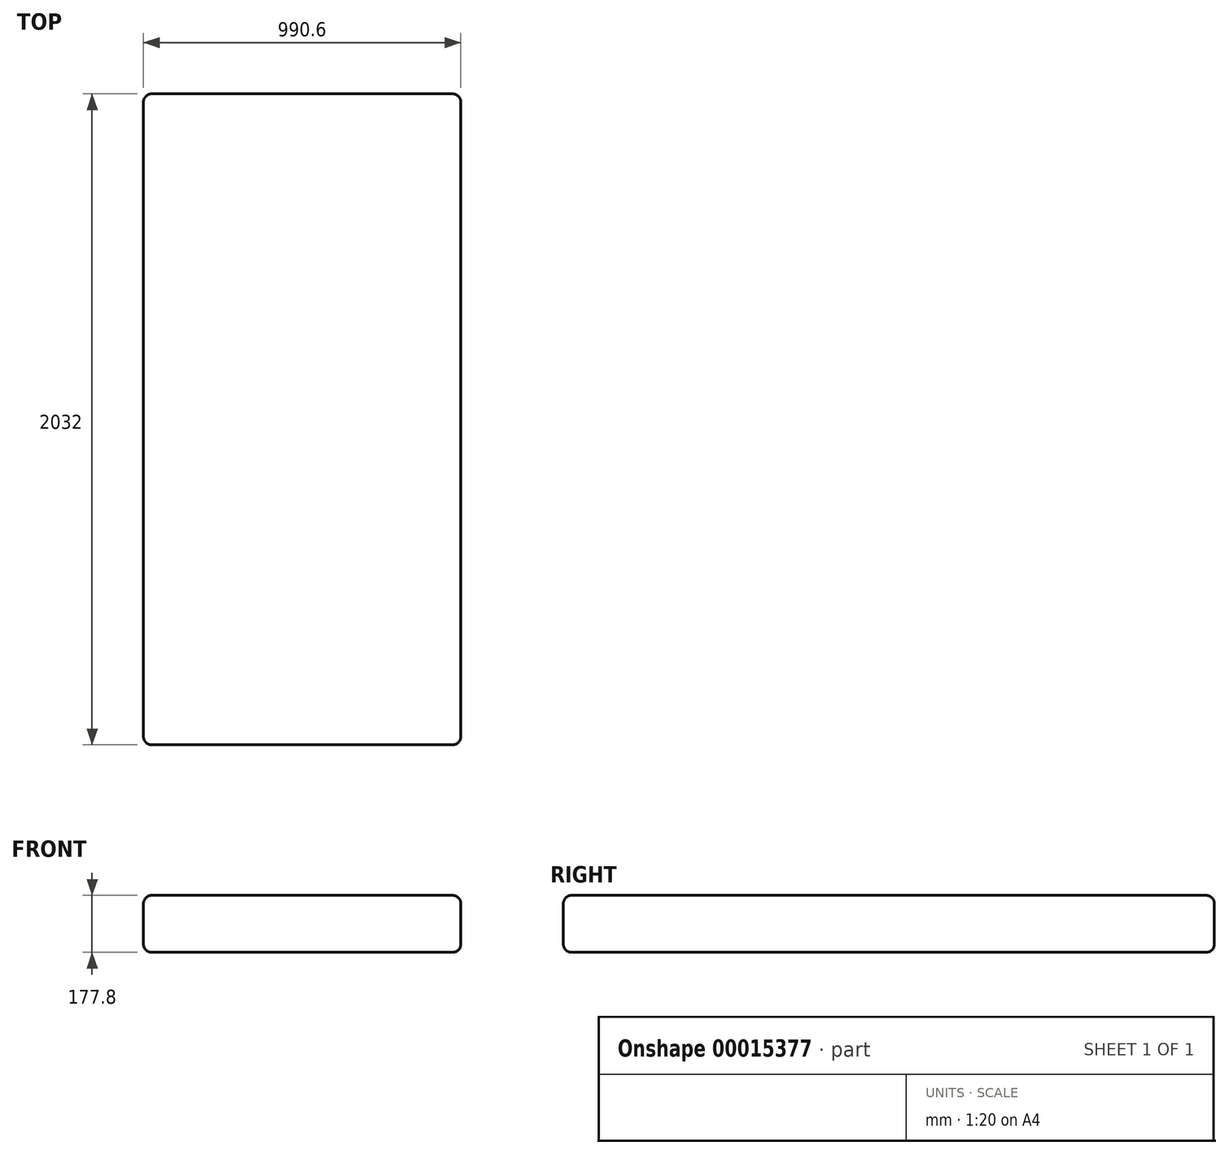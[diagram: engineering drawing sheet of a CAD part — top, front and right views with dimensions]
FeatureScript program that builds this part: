
annotation { "Feature Type Name" : "Feature", "Feature Type Description" : "" }
export const myFeature = defineFeature(function(context is Context, id is Id, definition is map)
    precondition{}
    {
        {
            var Q0;
            Q0=qCreatedBy(makeId("Top.planeOp"),FACE);
            var sketch = newSketch(context, id + "F0", { "sketchPlane" : qUnion([Q0])});
            skLineSegment(sketch, "E0.bottom", {"start": v(-495.25, -781.3) * mm, "end": v(495.35, -781.3) * mm});
            skLineSegment(sketch, "E0.top", {"start": v(-495.25, 1250.7) * mm, "end": v(495.35, 1250.7) * mm});
            skLineSegment(sketch, "E0.left", {"start": v(-495.25, -781.3) * mm, "end": v(-495.25, 1250.7) * mm});
            skLineSegment(sketch, "E0.right", {"start": v(495.35, -781.3) * mm, "end": v(495.35, 1250.7) * mm});
            skSolve(sketch);
        }
        {
            var Q0;
            Q0=qSketchRegion(id+"F0",true);
            extrude(context, id + "F1", {"entities" : qUnion([Q0]), "depth" : 177.8 * mm});
        }
        {
            var Q0;
            Q0=makeQuery(id+"F1.opExtrude","CAP_EDGE",EDGE,{"disambiguationData":[OSD([sQuery(id+"F0.wireOp",EDGE,"E0.bottom")])],"isStart":false});
            var Q1;
            Q1=makeQuery(id+"F1.opExtrude","CAP_EDGE",EDGE,{"disambiguationData":[OSD([sQuery(id+"F0.wireOp",EDGE,"E0.right")])],"isStart":false});
            var Q2;
            Q2=makeQuery(id+"F1.opExtrude","SWEPT_EDGE",EDGE,{"disambiguationData":[OSD([sQuery(id+"F0.wireOp",EDGE,"E0.bottom"),sQuery(id+"F0.wireOp",EDGE,"E0.right")])]});
            var Q3;
            Q3=makeQuery(id+"F1.opExtrude","SWEPT_EDGE",EDGE,{"disambiguationData":[OSD([sQuery(id+"F0.wireOp",EDGE,"E0.bottom"),sQuery(id+"F0.wireOp",EDGE,"E0.left")])]});
            var Q4;
            Q4=makeQuery(id+"F1.opExtrude","SWEPT_EDGE",EDGE,{"disambiguationData":[OSD([sQuery(id+"F0.wireOp",EDGE,"E0.top"),sQuery(id+"F0.wireOp",EDGE,"E0.left")])]});
            var Q5;
            Q5=makeQuery(id+"F1.opExtrude","SWEPT_EDGE",EDGE,{"disambiguationData":[OSD([sQuery(id+"F0.wireOp",EDGE,"E0.top"),sQuery(id+"F0.wireOp",EDGE,"E0.right")])]});
            var Q6;
            Q6=makeQuery(id+"F1.opExtrude","CAP_EDGE",EDGE,{"disambiguationData":[OSD([sQuery(id+"F0.wireOp",EDGE,"E0.bottom")])],"isStart":true});
            var Q7;
            Q7=makeQuery(id+"F1.opExtrude","CAP_EDGE",EDGE,{"disambiguationData":[OSD([sQuery(id+"F0.wireOp",EDGE,"E0.top")])],"isStart":false});
            var Q8;
            Q8=makeQuery(id+"F1.opExtrude","CAP_EDGE",EDGE,{"disambiguationData":[OSD([sQuery(id+"F0.wireOp",EDGE,"E0.left")])],"isStart":false});
            var Q9;
            Q9=makeQuery(id+"F1.opExtrude","CAP_EDGE",EDGE,{"disambiguationData":[OSD([sQuery(id+"F0.wireOp",EDGE,"E0.right")])],"isStart":true});
            var Q10;
            Q10=makeQuery(id+"F1.opExtrude","CAP_EDGE",EDGE,{"disambiguationData":[OSD([sQuery(id+"F0.wireOp",EDGE,"E0.top")])],"isStart":true});
            var Q11;
            Q11=makeQuery(id+"F1.opExtrude","CAP_EDGE",EDGE,{"disambiguationData":[OSD([sQuery(id+"F0.wireOp",EDGE,"E0.left")])],"isStart":true});
            fillet(context, id + "F2", {"entities" : qUnion([Q0, Q1, Q2, Q3, Q4, Q5, Q6, Q7, Q8, Q9, Q10, Q11]), "radius" : 25.4 * mm, "tangentPropagation" : true, "allowEdgeOverflow" : false});
        }
    });
